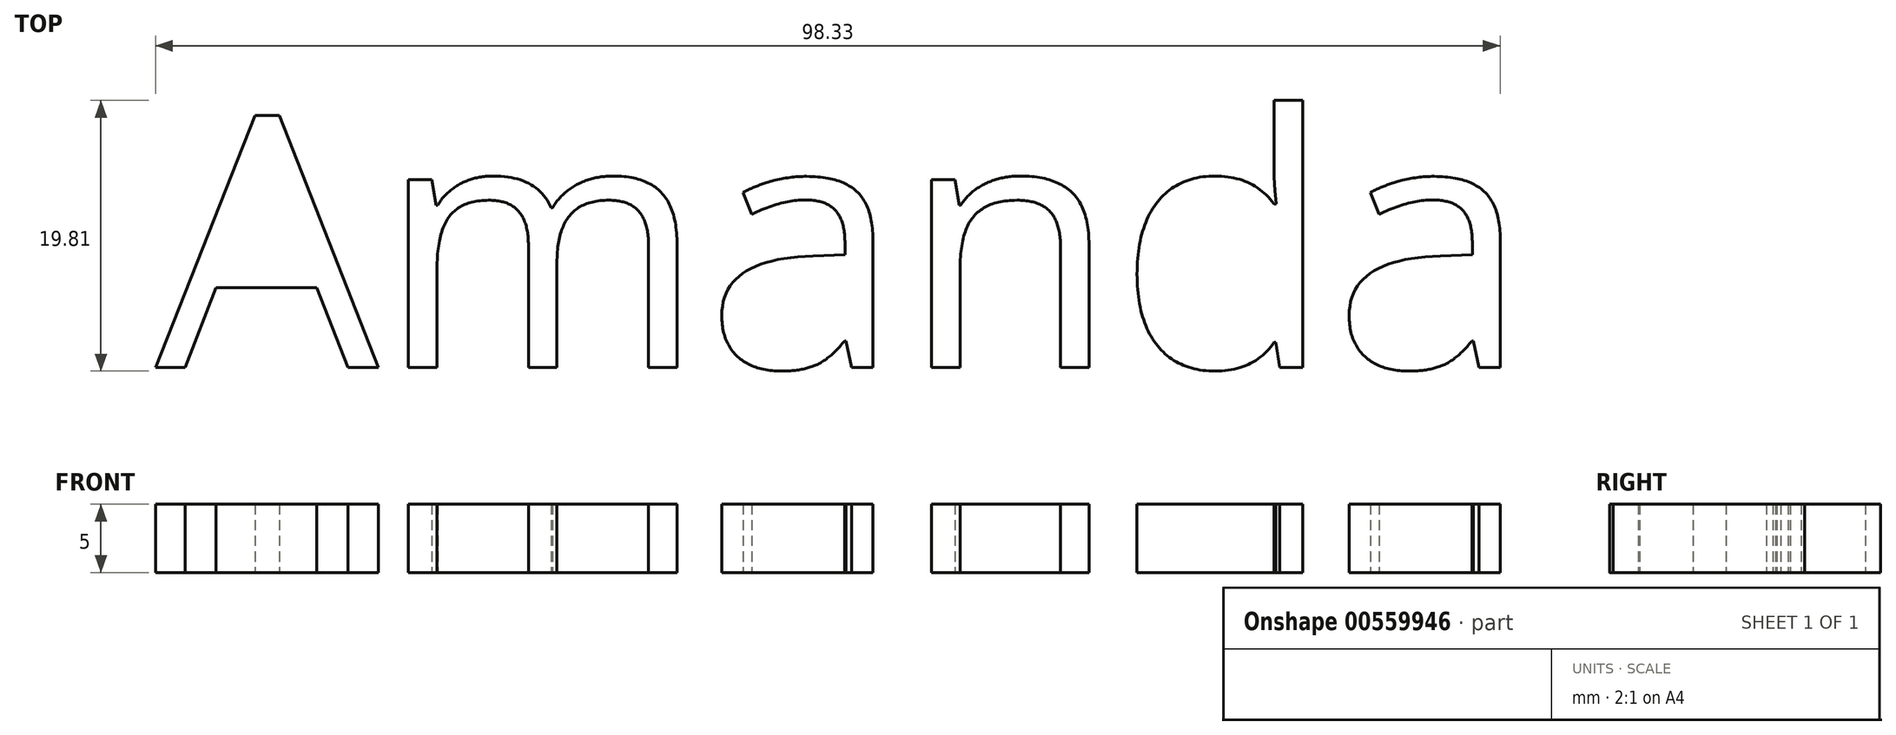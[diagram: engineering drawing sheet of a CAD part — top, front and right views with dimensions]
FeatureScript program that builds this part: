
annotation { "Feature Type Name" : "Feature", "Feature Type Description" : "" }
export const myFeature = defineFeature(function(context is Context, id is Id, definition is map)
    precondition{}
    {
        {
            var Q0;
            Q0=qCreatedBy(makeId("Top.planeOp"),FACE);
            var sketch = newSketch(context, id + "F0", { "sketchPlane" : qUnion([Q0])});
            skText(sketch, "E0", { "text": "Amanda", "fontName": "OpenSans-Regular.ttf"});
            const initialGuessF0  = {"E0": [-0.04987, -0.0084, 1, 0, 0.01853]};
            skSetInitialGuess(sketch, initialGuessF0);
            skSolve(sketch);
        }
        {
            var Q0;
            Q0 = qSketchRegion(id + "F0", true);
            var Q1;
            Q1=makeQuery(id+"F0.imprint","IMPRINT",FACE,{"disambiguationData":[TD([[makeQuery(id+"F0.imprint","IMPRINT",EDGE,{"derivedFrom":sQuery(id+"F0.wireOp",EDGE,"E0.sketch_text.stroke-128")}),1.0]])]});
            var Q2;
            Q2=makeQuery(id+"F0.imprint","IMPRINT",FACE,{"disambiguationData":[TD([[makeQuery(id+"F0.imprint","IMPRINT",EDGE,{"derivedFrom":sQuery(id+"F0.wireOp",EDGE,"E0.sketch_text.stroke-109")}),-1.0]])]});
            var Q3;
            Q3=makeQuery(id+"F0.imprint","IMPRINT",FACE,{"disambiguationData":[TD([[makeQuery(id+"F0.imprint","IMPRINT",EDGE,{"derivedFrom":sQuery(id+"F0.wireOp",EDGE,"E0.sketch_text.stroke-100")}),1.0]])]});
            var Q4;
            Q4=makeQuery(id+"F0.imprint","IMPRINT",FACE,{"disambiguationData":[TD([[makeQuery(id+"F0.imprint","IMPRINT",EDGE,{"derivedFrom":sQuery(id+"F0.wireOp",EDGE,"E0.sketch_text.stroke-85")}),-1.0]])]});
            var Q5;
            Q5=makeQuery(id+"F0.imprint","IMPRINT",FACE,{"disambiguationData":[TD([[makeQuery(id+"F0.imprint","IMPRINT",EDGE,{"derivedFrom":sQuery(id+"F0.wireOp",EDGE,"E0.sketch_text.stroke-41")}),-1.0]])]});
            var Q6;
            Q6=makeQuery(id+"F0.imprint","IMPRINT",FACE,{"disambiguationData":[TD([[makeQuery(id+"F0.imprint","IMPRINT",EDGE,{"derivedFrom":sQuery(id+"F0.wireOp",EDGE,"E0.sketch_text.stroke-8")}),1.0]])]});
            var Q7;
            Q7=makeQuery(id+"F0.imprint","IMPRINT",FACE,{"disambiguationData":[TD([[makeQuery(id+"F0.imprint","IMPRINT",EDGE,{"derivedFrom":sQuery(id+"F0.wireOp",EDGE,"E0.sketch_text.stroke-0")}),-1.0]])]});
            var Q8;
            Q8=makeQuery(id+"F0.imprint","IMPRINT",FACE,{"disambiguationData":[TD([[makeQuery(id+"F0.imprint","IMPRINT",EDGE,{"derivedFrom":sQuery(id+"F0.wireOp",EDGE,"E0.sketch_text.stroke-68")}),-1.0]])]});
            var Q9;
            Q9=makeQuery(id+"F0.imprint","IMPRINT",FACE,{"disambiguationData":[TD([[makeQuery(id+"F0.imprint","IMPRINT",EDGE,{"derivedFrom":sQuery(id+"F0.wireOp",EDGE,"E0.sketch_text.stroke-13")}),-1.0]])]});
            var Q10;
            Q10=makeQuery(id+"F0.imprint","IMPRINT",FACE,{"disambiguationData":[TD([[makeQuery(id+"F0.imprint","IMPRINT",EDGE,{"derivedFrom":sQuery(id+"F0.wireOp",EDGE,"E0.sketch_text.stroke-60")}),1.0]])]});
            extrude(context, id + "F1", {"entities" : qUnion([Q0, Q1, Q2, Q3, Q4, Q5, Q6, Q7, Q8, Q9, Q10]), "depth" : 5 * mm, "offsetDistance" : 25 * mm});
        }
    });
